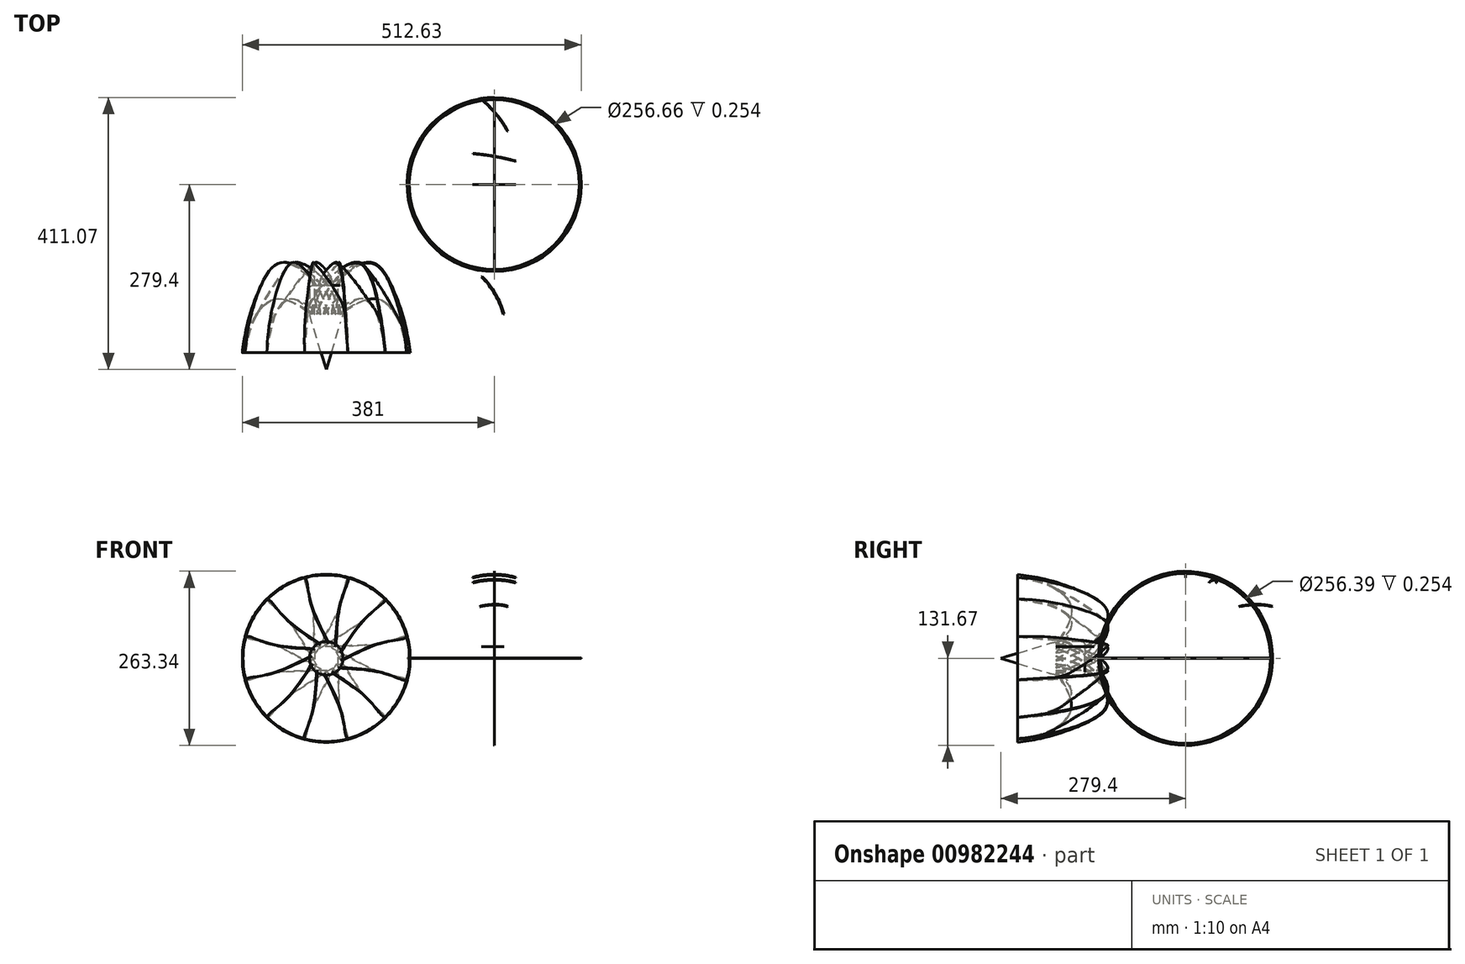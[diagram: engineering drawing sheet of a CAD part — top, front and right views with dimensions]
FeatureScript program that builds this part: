
annotation { "Feature Type Name" : "Feature", "Feature Type Description" : "" }
export const myFeature = defineFeature(function(context is Context, id is Id, definition is map)
    precondition{}
    {
        {
            var Q0;
            Q0=qCreatedBy(makeId("Front.planeOp"),FACE);
            var sketch = newSketch(context, id + "F0", { "sketchPlane" : qUnion([Q0])});
            skCircle(sketch, "E0", {"center": v(0, 0) * mm, "radius": 25.4 * mm});
            skCircle(sketch, "E1", {"center": v(0, 0) * mm, "radius": 127 * mm});
            skCircle(sketch, "E2", {"center": v(0, 0) * mm, "radius": 125.73 * mm});
            skLineSegment(sketch, "E3", {"start": v(0, 0) * mm, "end": v(32.87, 122.67) * mm});
            skLineSegment(sketch, "E4", {"start": v(0, 0) * mm, "end": v(-32.87, 122.67) * mm});
            skLineSegment(sketch, "E5", {"start": v(0, 0) * mm, "end": v(16.58, 125.91) * mm});
            skLineSegment(sketch, "E6", {"start": v(0, 0) * mm, "end": v(-16.58, 125.91) * mm});
            skSolve(sketch);
        }
        {
            var Q0;
            {var subQ0=sQuery(id+"F0.wireOp",EDGE,"E5");var subQ1=sQuery(id+"F0.wireOp",EDGE,"E1");var subQ2=makeQuery(id+"F0.imprint","INTERSECT",VERTEX,{"derivedFrom":[subQ1,subQ0]});Q0=makeQuery(id+"F0.imprint","IMPRINT",FACE,{"disambiguationData":[TD([[makeQuery(id+"F0.imprint","IMPRINT",EDGE,{"disambiguationData":[TD([[subQ2,-1.0]])],"derivedFrom":subQ1}),1.0]])]});}
            var Q1;
            {var subQ0=sQuery(id+"F0.wireOp",EDGE,"E4");var subQ1=sQuery(id+"F0.wireOp",EDGE,"E1");var subQ2=makeQuery(id+"F0.imprint","INTERSECT",VERTEX,{"derivedFrom":[subQ1,subQ0]});Q1=makeQuery(id+"F0.imprint","IMPRINT",FACE,{"disambiguationData":[TD([[makeQuery(id+"F0.imprint","IMPRINT",EDGE,{"disambiguationData":[TD([[subQ2,1.0]])],"derivedFrom":subQ1}),1.0]])]});}
            var Q2;
            {var subQ0=sQuery(id+"F0.wireOp",EDGE,"E3");var subQ1=sQuery(id+"F0.wireOp",EDGE,"E1");var subQ2=makeQuery(id+"F0.imprint","INTERSECT",VERTEX,{"derivedFrom":[subQ1,subQ0]});Q2=makeQuery(id+"F0.imprint","IMPRINT",FACE,{"disambiguationData":[TD([[makeQuery(id+"F0.imprint","IMPRINT",EDGE,{"disambiguationData":[TD([[subQ2,-1.0]])],"derivedFrom":subQ1}),1.0]])]});}
            extrude(context, id + "F1", {"entities" : qUnion([Q0, Q1, Q2]), "oppositeDirection" : true, "depth" : 0.13 * mm, "offsetDistance" : 25.4 * mm});
        }
        {
            var Q0;
            {var subQ0=sQuery(id+"F0.wireOp",EDGE,"E4");var subQ1=sQuery(id+"F0.wireOp",EDGE,"E1");var subQ2=makeQuery(id+"F0.imprint","INTERSECT",VERTEX,{"derivedFrom":[subQ1,subQ0]});Q0=makeQuery(id+"F0.imprint","IMPRINT",FACE,{"disambiguationData":[TD([[makeQuery(id+"F0.imprint","IMPRINT",EDGE,{"disambiguationData":[TD([[subQ2,1.0]])],"derivedFrom":subQ1}),1.0]])]});}
            var Q1;
            {var subQ0=sQuery(id+"F0.wireOp",EDGE,"E5");var subQ1=sQuery(id+"F0.wireOp",EDGE,"E1");var subQ2=makeQuery(id+"F0.imprint","INTERSECT",VERTEX,{"derivedFrom":[subQ1,subQ0]});Q1=makeQuery(id+"F0.imprint","IMPRINT",FACE,{"disambiguationData":[TD([[makeQuery(id+"F0.imprint","IMPRINT",EDGE,{"disambiguationData":[TD([[subQ2,-1.0]])],"derivedFrom":subQ1}),1.0]])]});}
            var Q2;
            {var subQ0=sQuery(id+"F0.wireOp",EDGE,"E3");var subQ1=sQuery(id+"F0.wireOp",EDGE,"E1");var subQ2=makeQuery(id+"F0.imprint","INTERSECT",VERTEX,{"derivedFrom":[subQ1,subQ0]});Q2=makeQuery(id+"F0.imprint","IMPRINT",FACE,{"disambiguationData":[TD([[makeQuery(id+"F0.imprint","IMPRINT",EDGE,{"disambiguationData":[TD([[subQ2,-1.0]])],"derivedFrom":subQ1}),1.0]])]});}
            extrude(context, id + "F2", {"entities" : qUnion([Q0, Q1, Q2]), "depth" : 0.13 * mm, "offsetDistance" : 25.4 * mm});
        }
        {
            var Q0;
            Q0=qCreatedBy(makeId("Top.planeOp"),FACE);
            var sketch = newSketch(context, id + "F3", { "sketchPlane" : qUnion([Q0])});
            skCircle(sketch, "E7", {"center": v(0, 0) * mm, "radius": 128.33 * mm});
            skCircle(sketch, "E8", {"center": v(0, 0) * mm, "radius": 131.63 * mm});
            skSolve(sketch);
        }
        {
            var Q0;
            Q0=makeQuery(id+"F3.imprint","IMPRINT",FACE,{"disambiguationData":[TD([[makeQuery(id+"F3.imprint","IMPRINT",EDGE,{"derivedFrom":sQuery(id+"F3.wireOp",EDGE,"E7")}),-1.0]])]});
            extrude(context, id + "F4", {"entities" : qUnion([Q0]), "depth" : 0.25 * mm, "offsetDistance" : 25.4 * mm});
        }
        {
            var Q0;
            Q0=qCreatedBy(makeId("Right.planeOp"),FACE);
            var sketch = newSketch(context, id + "F5", { "sketchPlane" : qUnion([Q0])});
            skCircle(sketch, "E9", {"center": v(0, 0) * mm, "radius": 128.2 * mm});
            skCircle(sketch, "E10", {"center": v(0, 0) * mm, "radius": 131.67 * mm});
            skSolve(sketch);
        }
        {
            var Q0;
            Q0=makeQuery(id+"F5.imprint","IMPRINT",FACE,{"disambiguationData":[TD([[makeQuery(id+"F5.imprint","IMPRINT",EDGE,{"derivedFrom":sQuery(id+"F5.wireOp",EDGE,"E9")}),-1.0]])]});
            extrude(context, id + "F6", {"entities" : qUnion([Q0]), "depth" : 0.25 * mm, "offsetDistance" : 25.4 * mm});
        }
        {
            var Q0;
            {var subQ0=sQuery(id+"F0.wireOp",EDGE,"E3");var subQ1=sQuery(id+"F0.wireOp",EDGE,"E0");var subQ2=makeQuery(id+"F0.imprint","INTERSECT",VERTEX,{"derivedFrom":[subQ1,subQ0]});Q0=makeQuery(id+"F0.imprint","IMPRINT",FACE,{"disambiguationData":[TD([[makeQuery(id+"F0.imprint","IMPRINT",EDGE,{"disambiguationData":[TD([[subQ2,1.0]])],"derivedFrom":subQ1}),1.0]])]});}
            var Q1;
            {var subQ0=sQuery(id+"F0.wireOp",EDGE,"E6");var subQ1=sQuery(id+"F0.wireOp",EDGE,"E0");var subQ2=makeQuery(id+"F0.imprint","INTERSECT",VERTEX,{"derivedFrom":[subQ1,subQ0]});Q1=makeQuery(id+"F0.imprint","IMPRINT",FACE,{"disambiguationData":[TD([[makeQuery(id+"F0.imprint","IMPRINT",EDGE,{"disambiguationData":[TD([[subQ2,-1.0]])],"derivedFrom":subQ1}),1.0]])]});}
            var Q2;
            {var subQ0=sQuery(id+"F0.wireOp",EDGE,"E5");var subQ1=sQuery(id+"F0.wireOp",EDGE,"E0");var subQ2=makeQuery(id+"F0.imprint","INTERSECT",VERTEX,{"derivedFrom":[subQ1,subQ0]});Q2=makeQuery(id+"F0.imprint","IMPRINT",FACE,{"disambiguationData":[TD([[makeQuery(id+"F0.imprint","IMPRINT",EDGE,{"disambiguationData":[TD([[subQ2,-1.0]])],"derivedFrom":subQ1}),1.0]])]});}
            var Q3;
            {var subQ0=sQuery(id+"F0.wireOp",EDGE,"E5");var subQ1=sQuery(id+"F0.wireOp",EDGE,"E0");var subQ2=makeQuery(id+"F0.imprint","INTERSECT",VERTEX,{"derivedFrom":[subQ1,subQ0]});Q3=makeQuery(id+"F0.imprint","IMPRINT",FACE,{"disambiguationData":[TD([[makeQuery(id+"F0.imprint","IMPRINT",EDGE,{"disambiguationData":[TD([[subQ2,1.0]])],"derivedFrom":subQ1}),1.0]])]});}
            extrude(context, id + "F7", {"entities" : qUnion([Q0, Q1, Q2, Q3]), "oppositeDirection" : true, "depth" : 127 * mm, "offsetDistance" : 25.4 * mm});
        }
        {
            var Q0;
            Q0=makeQuery(id+"F7.opExtrude","SWEPT_BODY",BODY,{"disambiguationData":[OSD([sQuery(id+"F0.wireOp",EDGE,"E0")])]});
            transform(context, id + "F8", {"entities" : qUnion([Q0]), "transformType" : TransformType.TRANSLATION_3D, "dx" : 0 * mm, "dy" : 203.2 * mm, "dz" : 0 * mm, "makeCopy" : false});
        }
        {
            var Q0;
            Q0=makeQuery(id+"F1.opExtrude","SWEPT_BODY",BODY,{"disambiguationData":[OSD([sQuery(id+"F0.wireOp",EDGE,"E1"),sQuery(id+"F0.wireOp",EDGE,"E2"),sQuery(id+"F0.wireOp",EDGE,"E5"),sQuery(id+"F0.wireOp",EDGE,"E6")])]});
            var Q1;
            Q1=makeQuery(id+"F6.opExtrude","CAP_EDGE",EDGE,{"disambiguationData":[OSD([sQuery(id+"F5.wireOp",EDGE,"E9")])],"isStart":false});
            transform(context, id + "F9", {"entities" : qUnion([Q0]), "transformType" : TransformType.ROTATION, "transformAxis" : qUnion([Q1]), "angle" : 90 * degree, "oppositeDirection" : true, "makeCopy" : true});
        }
        {
            var Q0;
            Q0=makeQuery(id+"F9.opPattern","COPY",BODY,{"derivedFrom":makeQuery(id+"F1.opExtrude","SWEPT_BODY",BODY,{"disambiguationData":[OSD([sQuery(id+"F0.wireOp",EDGE,"E1"),sQuery(id+"F0.wireOp",EDGE,"E2"),sQuery(id+"F0.wireOp",EDGE,"E5"),sQuery(id+"F0.wireOp",EDGE,"E6")])]}),"instanceName":"1"});
            var Q1;
            Q1=makeQuery(id+"F4.opExtrude","CAP_EDGE",EDGE,{"disambiguationData":[OSD([sQuery(id+"F3.wireOp",EDGE,"E7")])],"isStart":false});
            transform(context, id + "F10", {"entities" : qUnion([Q0]), "transformType" : TransformType.ROTATION, "transformAxis" : qUnion([Q1]), "angle" : 60 * degree, "oppositeDirection" : true, "makeCopy" : false});
        }
        {
            var Q0;
            Q0=makeQuery(id+"F9.opPattern","COPY",BODY,{"derivedFrom":makeQuery(id+"F1.opExtrude","SWEPT_BODY",BODY,{"disambiguationData":[OSD([sQuery(id+"F0.wireOp",EDGE,"E1"),sQuery(id+"F0.wireOp",EDGE,"E2"),sQuery(id+"F0.wireOp",EDGE,"E5"),sQuery(id+"F0.wireOp",EDGE,"E6")])]}),"instanceName":"1"});
            transform(context, id + "F11", {"entities" : qUnion([Q0]), "transformType" : TransformType.TRANSLATION_3D, "dx" : -107.95 * mm, "dy" : 25.4 * mm, "dz" : 0 * mm, "makeCopy" : false});
        }
        {
            var Q0;
            Q0=makeQuery(id+"F1.opExtrude","SWEPT_BODY",BODY,{"disambiguationData":[OSD([sQuery(id+"F0.wireOp",EDGE,"E1"),sQuery(id+"F0.wireOp",EDGE,"E2"),sQuery(id+"F0.wireOp",EDGE,"E5"),sQuery(id+"F0.wireOp",EDGE,"E6")])]});
            var Q1;
            Q1=makeQuery(id+"F6.opExtrude","CAP_EDGE",EDGE,{"disambiguationData":[OSD([sQuery(id+"F5.wireOp",EDGE,"E9")])],"isStart":false});
            transform(context, id + "F12", {"entities" : qUnion([Q0]), "transformType" : TransformType.ROTATION, "transformAxis" : qUnion([Q1]), "angle" : 20 * degree, "oppositeDirection" : true, "makeCopy" : false});
        }
        {
            var Q0;
            Q0=makeQuery(id+"F1.opExtrude","SWEPT_BODY",BODY,{"disambiguationData":[OSD([sQuery(id+"F0.wireOp",EDGE,"E1"),sQuery(id+"F0.wireOp",EDGE,"E2"),sQuery(id+"F0.wireOp",EDGE,"E5"),sQuery(id+"F0.wireOp",EDGE,"E6")])]});
            var Q1;
            Q1=makeQuery(id+"F6.opExtrude","CAP_EDGE",EDGE,{"disambiguationData":[OSD([sQuery(id+"F5.wireOp",EDGE,"E9")])],"isStart":false});
            transform(context, id + "F13", {"entities" : qUnion([Q0]), "transformType" : TransformType.ROTATION, "transformAxis" : qUnion([Q1]), "angle" : 30 * degree, "oppositeDirection" : true, "makeCopy" : true});
        }
        {
            var Q0;
            Q0=makeQuery(id+"F1.opExtrude","SWEPT_BODY",BODY,{"disambiguationData":[OSD([sQuery(id+"F0.wireOp",EDGE,"E1"),sQuery(id+"F0.wireOp",EDGE,"E2"),sQuery(id+"F0.wireOp",EDGE,"E5"),sQuery(id+"F0.wireOp",EDGE,"E6")])]});
            var Q1;
            Q1=makeQuery(id+"F4.opExtrude","CAP_EDGE",EDGE,{"disambiguationData":[OSD([sQuery(id+"F3.wireOp",EDGE,"E7")])],"isStart":false});
            transform(context, id + "F14", {"entities" : qUnion([Q0]), "transformType" : TransformType.ROTATION, "transformAxis" : qUnion([Q1]), "angle" : 10 * degree, "oppositeDirection" : true, "makeCopy" : false});
        }
        {
            var Q0;
            Q0=makeQuery(id+"F1.opExtrude","SWEPT_BODY",BODY,{"disambiguationData":[OSD([sQuery(id+"F0.wireOp",EDGE,"E1"),sQuery(id+"F0.wireOp",EDGE,"E2"),sQuery(id+"F0.wireOp",EDGE,"E5"),sQuery(id+"F0.wireOp",EDGE,"E6")])]});
            transform(context, id + "F15", {"entities" : qUnion([Q0]), "transformType" : TransformType.TRANSLATION_3D, "dx" : -7.11 * mm, "dy" : 0 * mm, "dz" : 0 * mm, "makeCopy" : false});
        }
        {
            var Q0;
            Q0=makeQuery(id+"F13.opPattern","COPY",BODY,{"derivedFrom":makeQuery(id+"F1.opExtrude","SWEPT_BODY",BODY,{"disambiguationData":[OSD([sQuery(id+"F0.wireOp",EDGE,"E1"),sQuery(id+"F0.wireOp",EDGE,"E2"),sQuery(id+"F0.wireOp",EDGE,"E5"),sQuery(id+"F0.wireOp",EDGE,"E6")])]}),"instanceName":"1"});
            var Q1;
            Q1=makeQuery(id+"F4.opExtrude","CAP_EDGE",EDGE,{"disambiguationData":[OSD([sQuery(id+"F3.wireOp",EDGE,"E7")])],"isStart":false});
            transform(context, id + "F16", {"entities" : qUnion([Q0]), "transformType" : TransformType.ROTATION, "transformAxis" : qUnion([Q1]), "angle" : 50 * degree, "oppositeDirection" : true, "makeCopy" : false});
        }
        {
            var Q0;
            Q0=makeQuery(id+"F13.opPattern","COPY",BODY,{"derivedFrom":makeQuery(id+"F1.opExtrude","SWEPT_BODY",BODY,{"disambiguationData":[OSD([sQuery(id+"F0.wireOp",EDGE,"E1"),sQuery(id+"F0.wireOp",EDGE,"E2"),sQuery(id+"F0.wireOp",EDGE,"E5"),sQuery(id+"F0.wireOp",EDGE,"E6")])]}),"instanceName":"1"});
            transform(context, id + "F17", {"entities" : qUnion([Q0]), "transformType" : TransformType.TRANSLATION_3D, "dx" : -72.39 * mm, "dy" : 45.72 * mm, "dz" : 0 * mm, "makeCopy" : false});
        }
        {
            var Q0;
            Q0=makeQuery(id+"F9.opPattern","COPY",BODY,{"derivedFrom":makeQuery(id+"F1.opExtrude","SWEPT_BODY",BODY,{"disambiguationData":[OSD([sQuery(id+"F0.wireOp",EDGE,"E1"),sQuery(id+"F0.wireOp",EDGE,"E2"),sQuery(id+"F0.wireOp",EDGE,"E5"),sQuery(id+"F0.wireOp",EDGE,"E6")])]}),"instanceName":"1"});
            transform(context, id + "F18", {"entities" : qUnion([Q0]), "transformType" : TransformType.TRANSLATION_3D, "dx" : 0 * mm, "dy" : 0 * mm, "dz" : 17.78 * mm, "makeCopy" : false});
        }
        {
            var Q0;
            Q0=makeQuery(id+"F2.opExtrude","CAP_FACE",FACE,{"disambiguationData":[OSD([sQuery(id+"F0.wireOp",EDGE,"E1"),sQuery(id+"F0.wireOp",EDGE,"E2"),sQuery(id+"F0.wireOp",EDGE,"E3"),sQuery(id+"F0.wireOp",EDGE,"E4")])],"isStart":false});
            var Q1;
            Q1=makeQuery(id+"F1.opExtrude","CAP_FACE",FACE,{"disambiguationData":[OSD([sQuery(id+"F0.wireOp",EDGE,"E1"),sQuery(id+"F0.wireOp",EDGE,"E2"),sQuery(id+"F0.wireOp",EDGE,"E5"),sQuery(id+"F0.wireOp",EDGE,"E6")])],"isStart":true});
            var Q2;
            Q2=makeQuery(id+"F13.opPattern","COPY",FACE,{"derivedFrom":makeQuery(id+"F1.opExtrude","CAP_FACE",FACE,{"disambiguationData":[OSD([sQuery(id+"F0.wireOp",EDGE,"E1"),sQuery(id+"F0.wireOp",EDGE,"E2"),sQuery(id+"F0.wireOp",EDGE,"E5"),sQuery(id+"F0.wireOp",EDGE,"E6")])],"isStart":true}),"instanceName":"1"});
            var Q3;
            Q3=makeQuery(id+"F9.opPattern","COPY",FACE,{"derivedFrom":makeQuery(id+"F1.opExtrude","CAP_FACE",FACE,{"disambiguationData":[OSD([sQuery(id+"F0.wireOp",EDGE,"E1"),sQuery(id+"F0.wireOp",EDGE,"E2"),sQuery(id+"F0.wireOp",EDGE,"E5"),sQuery(id+"F0.wireOp",EDGE,"E6")])],"isStart":true}),"instanceName":"1"});
            loft(context, id + "F19", {"sheetProfilesArray" : [{ "sheetProfileEntities" : qUnion([Q0]) }, { "sheetProfileEntities" : qUnion([Q1]) }, { "sheetProfileEntities" : qUnion([Q2]) }, { "sheetProfileEntities" : qUnion([Q3]) }]});
        }
        {
            var Q0;
            Q0=makeQuery(id+"F7.opExtrude","SWEPT_BODY",BODY,{"disambiguationData":[OSD([sQuery(id+"F0.wireOp",EDGE,"E0")])]});
            transform(context, id + "F20", {"entities" : qUnion([Q0]), "transformType" : TransformType.TRANSLATION_3D, "dx" : 0 * mm, "dy" : -228.6 * mm, "dz" : 0 * mm, "makeCopy" : false});
        }
        {
            var Q0;
            Q0=makeQuery(id+"F7.opExtrude","CAP_EDGE",EDGE,{"disambiguationData":[OSD([sQuery(id+"F0.wireOp",EDGE,"E0")])],"isStart":true});
            chamfer(context, id + "F21", {"entities" : qUnion([Q0]), "chamferType" : ChamferType.TWO_OFFSETS, "width1" : 25.4 * mm, "oppositeDirection" : false, "width2" : 82.55 * mm, "tangentPropagation" : true});
        }
        {
            var Q0;
            Q0=makeQuery(id+"F6.opExtrude","SWEPT_BODY",BODY,{"disambiguationData":[OSD([sQuery(id+"F5.wireOp",EDGE,"E9"),sQuery(id+"F5.wireOp",EDGE,"E10")])]});
            var Q1;
            Q1=makeQuery(id+"F4.opExtrude","SWEPT_BODY",BODY,{"disambiguationData":[OSD([sQuery(id+"F3.wireOp",EDGE,"E7"),sQuery(id+"F3.wireOp",EDGE,"E8")])]});
            var Q2;
            Q2=makeQuery(id+"F2.opExtrude","SWEPT_BODY",BODY,{"disambiguationData":[OSD([sQuery(id+"F0.wireOp",EDGE,"E1"),sQuery(id+"F0.wireOp",EDGE,"E2"),sQuery(id+"F0.wireOp",EDGE,"E3"),sQuery(id+"F0.wireOp",EDGE,"E4")])]});
            var Q3;
            Q3=makeQuery(id+"F1.opExtrude","SWEPT_BODY",BODY,{"disambiguationData":[OSD([sQuery(id+"F0.wireOp",EDGE,"E1"),sQuery(id+"F0.wireOp",EDGE,"E2"),sQuery(id+"F0.wireOp",EDGE,"E5"),sQuery(id+"F0.wireOp",EDGE,"E6")])]});
            var Q4;
            Q4=makeQuery(id+"F13.opPattern","COPY",BODY,{"derivedFrom":makeQuery(id+"F1.opExtrude","SWEPT_BODY",BODY,{"disambiguationData":[OSD([sQuery(id+"F0.wireOp",EDGE,"E1"),sQuery(id+"F0.wireOp",EDGE,"E2"),sQuery(id+"F0.wireOp",EDGE,"E5"),sQuery(id+"F0.wireOp",EDGE,"E6")])]}),"instanceName":"1"});
            transform(context, id + "F22", {"entities" : qUnion([Q0, Q1, Q2, Q3, Q4]), "transformType" : TransformType.TRANSLATION_3D, "dx" : 254 * mm, "dy" : 254 * mm, "dz" : 0 * mm, "makeCopy" : false});
        }
        {
            var Q0;
            Q0=makeQuery(id+"F19.opLoft","SWEPT_BODY",BODY,{"disambiguationData":[OSD([sQuery(id+"F0.wireOp",EDGE,"E1"),sQuery(id+"F0.wireOp",EDGE,"E2"),sQuery(id+"F0.wireOp",EDGE,"E3"),sQuery(id+"F0.wireOp",EDGE,"E4"),sQuery(id+"F0.wireOp",EDGE,"E5"),sQuery(id+"F0.wireOp",EDGE,"E6")])]});
            var Q1;
            {var subQ0=sQuery(id+"F0.wireOp",EDGE,"E0");Q1=makeQuery(id+"F21.opChamfer","BLEND_EDGE",EDGE,{"blendedFrom":[makeQuery(id+"F7.opExtrude","CAP_EDGE",EDGE,{"disambiguationData":[OSD([subQ0])],"isStart":true}),makeQuery(id+"F7.opExtrude","SWEPT_FACE",FACE,{"disambiguationData":[OSD([subQ0])]})],"blendedInto":[makeQuery(id+"F7.opExtrude","SWEPT_FACE",FACE,{"disambiguationData":[OSD([subQ0])]})]});}
            transform(context, id + "F23", {"entities" : qUnion([Q0]), "transformType" : TransformType.ROTATION, "transformAxis" : qUnion([Q1]), "angle" : 30 * degree, "makeCopy" : true});
        }
        {
            var Q0;
            Q0=makeQuery(id+"F19.opLoft","SWEPT_BODY",BODY,{"disambiguationData":[OSD([sQuery(id+"F0.wireOp",EDGE,"E1"),sQuery(id+"F0.wireOp",EDGE,"E2"),sQuery(id+"F0.wireOp",EDGE,"E3"),sQuery(id+"F0.wireOp",EDGE,"E4"),sQuery(id+"F0.wireOp",EDGE,"E5"),sQuery(id+"F0.wireOp",EDGE,"E6")])]});
            var Q1;
            Q1=makeQuery(id+"F23.opPattern","COPY",BODY,{"derivedFrom":makeQuery(id+"F19.opLoft","SWEPT_BODY",BODY,{"disambiguationData":[OSD([sQuery(id+"F0.wireOp",EDGE,"E1"),sQuery(id+"F0.wireOp",EDGE,"E2"),sQuery(id+"F0.wireOp",EDGE,"E3"),sQuery(id+"F0.wireOp",EDGE,"E4"),sQuery(id+"F0.wireOp",EDGE,"E5"),sQuery(id+"F0.wireOp",EDGE,"E6")])]}),"instanceName":"1"});
            var Q2;
            {var subQ0=sQuery(id+"F0.wireOp",EDGE,"E0");Q2=makeQuery(id+"F21.opChamfer","BLEND_EDGE",EDGE,{"blendedFrom":[makeQuery(id+"F7.opExtrude","CAP_EDGE",EDGE,{"disambiguationData":[OSD([subQ0])],"isStart":true}),makeQuery(id+"F7.opExtrude","SWEPT_FACE",FACE,{"disambiguationData":[OSD([subQ0])]})],"blendedInto":[makeQuery(id+"F7.opExtrude","SWEPT_FACE",FACE,{"disambiguationData":[OSD([subQ0])]})]});}
            transform(context, id + "F24", {"entities" : qUnion([Q0, Q1]), "transformType" : TransformType.ROTATION, "transformAxis" : qUnion([Q2]), "angle" : 60 * degree, "makeCopy" : true});
        }
        {
            var Q0;
            Q0=makeQuery(id+"F19.opLoft","SWEPT_BODY",BODY,{"disambiguationData":[OSD([sQuery(id+"F0.wireOp",EDGE,"E1"),sQuery(id+"F0.wireOp",EDGE,"E2"),sQuery(id+"F0.wireOp",EDGE,"E3"),sQuery(id+"F0.wireOp",EDGE,"E4"),sQuery(id+"F0.wireOp",EDGE,"E5"),sQuery(id+"F0.wireOp",EDGE,"E6")])]});
            var Q1;
            Q1=makeQuery(id+"F23.opPattern","COPY",BODY,{"derivedFrom":makeQuery(id+"F19.opLoft","SWEPT_BODY",BODY,{"disambiguationData":[OSD([sQuery(id+"F0.wireOp",EDGE,"E1"),sQuery(id+"F0.wireOp",EDGE,"E2"),sQuery(id+"F0.wireOp",EDGE,"E3"),sQuery(id+"F0.wireOp",EDGE,"E4"),sQuery(id+"F0.wireOp",EDGE,"E5"),sQuery(id+"F0.wireOp",EDGE,"E6")])]}),"instanceName":"1"});
            var Q2;
            Q2=makeQuery(id+"F24.opPattern","COPY",BODY,{"derivedFrom":makeQuery(id+"F19.opLoft","SWEPT_BODY",BODY,{"disambiguationData":[OSD([sQuery(id+"F0.wireOp",EDGE,"E1"),sQuery(id+"F0.wireOp",EDGE,"E2"),sQuery(id+"F0.wireOp",EDGE,"E3"),sQuery(id+"F0.wireOp",EDGE,"E4"),sQuery(id+"F0.wireOp",EDGE,"E5"),sQuery(id+"F0.wireOp",EDGE,"E6")])]}),"instanceName":"1"});
            var Q3;
            Q3=makeQuery(id+"F24.opPattern","COPY",BODY,{"derivedFrom":makeQuery(id+"F23.opPattern","COPY",BODY,{"derivedFrom":makeQuery(id+"F19.opLoft","SWEPT_BODY",BODY,{"disambiguationData":[OSD([sQuery(id+"F0.wireOp",EDGE,"E1"),sQuery(id+"F0.wireOp",EDGE,"E2"),sQuery(id+"F0.wireOp",EDGE,"E3"),sQuery(id+"F0.wireOp",EDGE,"E4"),sQuery(id+"F0.wireOp",EDGE,"E5"),sQuery(id+"F0.wireOp",EDGE,"E6")])]}),"instanceName":"1"}),"instanceName":"1"});
            var Q4;
            {var subQ0=sQuery(id+"F0.wireOp",EDGE,"E0");Q4=makeQuery(id+"F21.opChamfer","BLEND_EDGE",EDGE,{"blendedFrom":[makeQuery(id+"F7.opExtrude","CAP_EDGE",EDGE,{"disambiguationData":[OSD([subQ0])],"isStart":true}),makeQuery(id+"F7.opExtrude","SWEPT_FACE",FACE,{"disambiguationData":[OSD([subQ0])]})],"blendedInto":[makeQuery(id+"F7.opExtrude","SWEPT_FACE",FACE,{"disambiguationData":[OSD([subQ0])]})]});}
            transform(context, id + "F25", {"entities" : qUnion([Q0, Q1, Q2, Q3]), "transformType" : TransformType.ROTATION, "transformAxis" : qUnion([Q4]), "angle" : 120 * degree, "makeCopy" : true});
        }
        {
            var Q0;
            Q0=makeQuery(id+"F25.opPattern","COPY",BODY,{"derivedFrom":makeQuery(id+"F24.opPattern","COPY",BODY,{"derivedFrom":makeQuery(id+"F23.opPattern","COPY",BODY,{"derivedFrom":makeQuery(id+"F19.opLoft","SWEPT_BODY",BODY,{"disambiguationData":[OSD([sQuery(id+"F0.wireOp",EDGE,"E1"),sQuery(id+"F0.wireOp",EDGE,"E2"),sQuery(id+"F0.wireOp",EDGE,"E3"),sQuery(id+"F0.wireOp",EDGE,"E4"),sQuery(id+"F0.wireOp",EDGE,"E5"),sQuery(id+"F0.wireOp",EDGE,"E6")])]}),"instanceName":"1"}),"instanceName":"1"}),"instanceName":"1"});
            var Q1;
            Q1=makeQuery(id+"F25.opPattern","COPY",BODY,{"derivedFrom":makeQuery(id+"F24.opPattern","COPY",BODY,{"derivedFrom":makeQuery(id+"F19.opLoft","SWEPT_BODY",BODY,{"disambiguationData":[OSD([sQuery(id+"F0.wireOp",EDGE,"E1"),sQuery(id+"F0.wireOp",EDGE,"E2"),sQuery(id+"F0.wireOp",EDGE,"E3"),sQuery(id+"F0.wireOp",EDGE,"E4"),sQuery(id+"F0.wireOp",EDGE,"E5"),sQuery(id+"F0.wireOp",EDGE,"E6")])]}),"instanceName":"1"}),"instanceName":"1"});
            var Q2;
            Q2=makeQuery(id+"F25.opPattern","COPY",BODY,{"derivedFrom":makeQuery(id+"F23.opPattern","COPY",BODY,{"derivedFrom":makeQuery(id+"F19.opLoft","SWEPT_BODY",BODY,{"disambiguationData":[OSD([sQuery(id+"F0.wireOp",EDGE,"E1"),sQuery(id+"F0.wireOp",EDGE,"E2"),sQuery(id+"F0.wireOp",EDGE,"E3"),sQuery(id+"F0.wireOp",EDGE,"E4"),sQuery(id+"F0.wireOp",EDGE,"E5"),sQuery(id+"F0.wireOp",EDGE,"E6")])]}),"instanceName":"1"}),"instanceName":"1"});
            var Q3;
            Q3=makeQuery(id+"F25.opPattern","COPY",BODY,{"derivedFrom":makeQuery(id+"F19.opLoft","SWEPT_BODY",BODY,{"disambiguationData":[OSD([sQuery(id+"F0.wireOp",EDGE,"E1"),sQuery(id+"F0.wireOp",EDGE,"E2"),sQuery(id+"F0.wireOp",EDGE,"E3"),sQuery(id+"F0.wireOp",EDGE,"E4"),sQuery(id+"F0.wireOp",EDGE,"E5"),sQuery(id+"F0.wireOp",EDGE,"E6")])]}),"instanceName":"1"});
            var Q4;
            {var subQ0=sQuery(id+"F0.wireOp",EDGE,"E0");Q4=makeQuery(id+"F21.opChamfer","BLEND_EDGE",EDGE,{"blendedFrom":[makeQuery(id+"F7.opExtrude","CAP_EDGE",EDGE,{"disambiguationData":[OSD([subQ0])],"isStart":true}),makeQuery(id+"F7.opExtrude","SWEPT_FACE",FACE,{"disambiguationData":[OSD([subQ0])]})],"blendedInto":[makeQuery(id+"F7.opExtrude","SWEPT_FACE",FACE,{"disambiguationData":[OSD([subQ0])]})]});}
            transform(context, id + "F26", {"entities" : qUnion([Q0, Q1, Q2, Q3]), "transformType" : TransformType.ROTATION, "transformAxis" : qUnion([Q4]), "angle" : 120 * degree, "makeCopy" : true});
        }
        {
            var Q0;
            {var subQ0=sQuery(id+"F0.wireOp",EDGE,"E0");Q0=makeQuery(id+"F21.opChamfer","BLEND_EDGE",EDGE,{"blendedFrom":[makeQuery(id+"F7.opExtrude","CAP_EDGE",EDGE,{"disambiguationData":[OSD([subQ0])],"isStart":true}),makeQuery(id+"F7.opExtrude","SWEPT_FACE",FACE,{"disambiguationData":[OSD([subQ0])]})],"blendedInto":[makeQuery(id+"F7.opExtrude","SWEPT_FACE",FACE,{"disambiguationData":[OSD([subQ0])]})]});}
            fillet(context, id + "F27", {"entities" : qUnion([Q0]), "radius" : 76.2 * mm, "tangentPropagation" : true, "allowEdgeOverflow" : false});
        }
        {
            var Q0;
            Q0=makeQuery(id+"F9.opPattern","COPY",BODY,{"derivedFrom":makeQuery(id+"F1.opExtrude","SWEPT_BODY",BODY,{"disambiguationData":[OSD([sQuery(id+"F0.wireOp",EDGE,"E1"),sQuery(id+"F0.wireOp",EDGE,"E2"),sQuery(id+"F0.wireOp",EDGE,"E3"),sQuery(id+"F0.wireOp",EDGE,"E4")])]}),"instanceName":"1"});
            transform(context, id + "F28", {"entities" : qUnion([Q0]), "transformType" : TransformType.TRANSLATION_3D, "dx" : 254 * mm, "dy" : 0 * mm, "dz" : 0 * mm, "makeCopy" : false});
        }
        {
            var Q0;
            Q0=makeQuery(id+"F7.opExtrude","CAP_EDGE",EDGE,{"disambiguationData":[OSD([sQuery(id+"F0.wireOp",EDGE,"E0")])],"isStart":false});
            fillet(context, id + "F29", {"entities" : qUnion([Q0]), "radius" : 5.08 * mm, "tangentPropagation" : true, "allowEdgeOverflow" : false});
        }
    });
